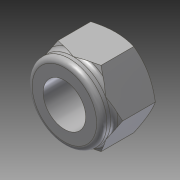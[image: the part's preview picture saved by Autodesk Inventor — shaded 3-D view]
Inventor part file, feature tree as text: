
AUTODESK INVENTOR PART (.ipt)
format: ipt  version: 2014 SP1 (Build 180222100, 222)  size: 162,304 bytes
history: native  units: in
note: dims shown in document units (in); Inventor stores cm internally (conversion verified against a paired STEP export)
features: fillet x1, other x1, imported_body x1
ambient origin geometry x8: Origin, YZ Plane, XZ Plane, XY Plane, X Axis, Y Axis, Z Axis, Center Point
bodies: Body1 (feature_tree)
feature tree (3):
  fillet  "Fillet7"  [1 undecoded]
  other  "Nylock Nut_NNY2520-ZC.ipt1"
  imported_body  "Base1"
note: 1 required parameter value undecoded (feature->parameter linkage not recoverable at this tier; creation-order binding heuristic only, values carry confidence <= 0.55)
